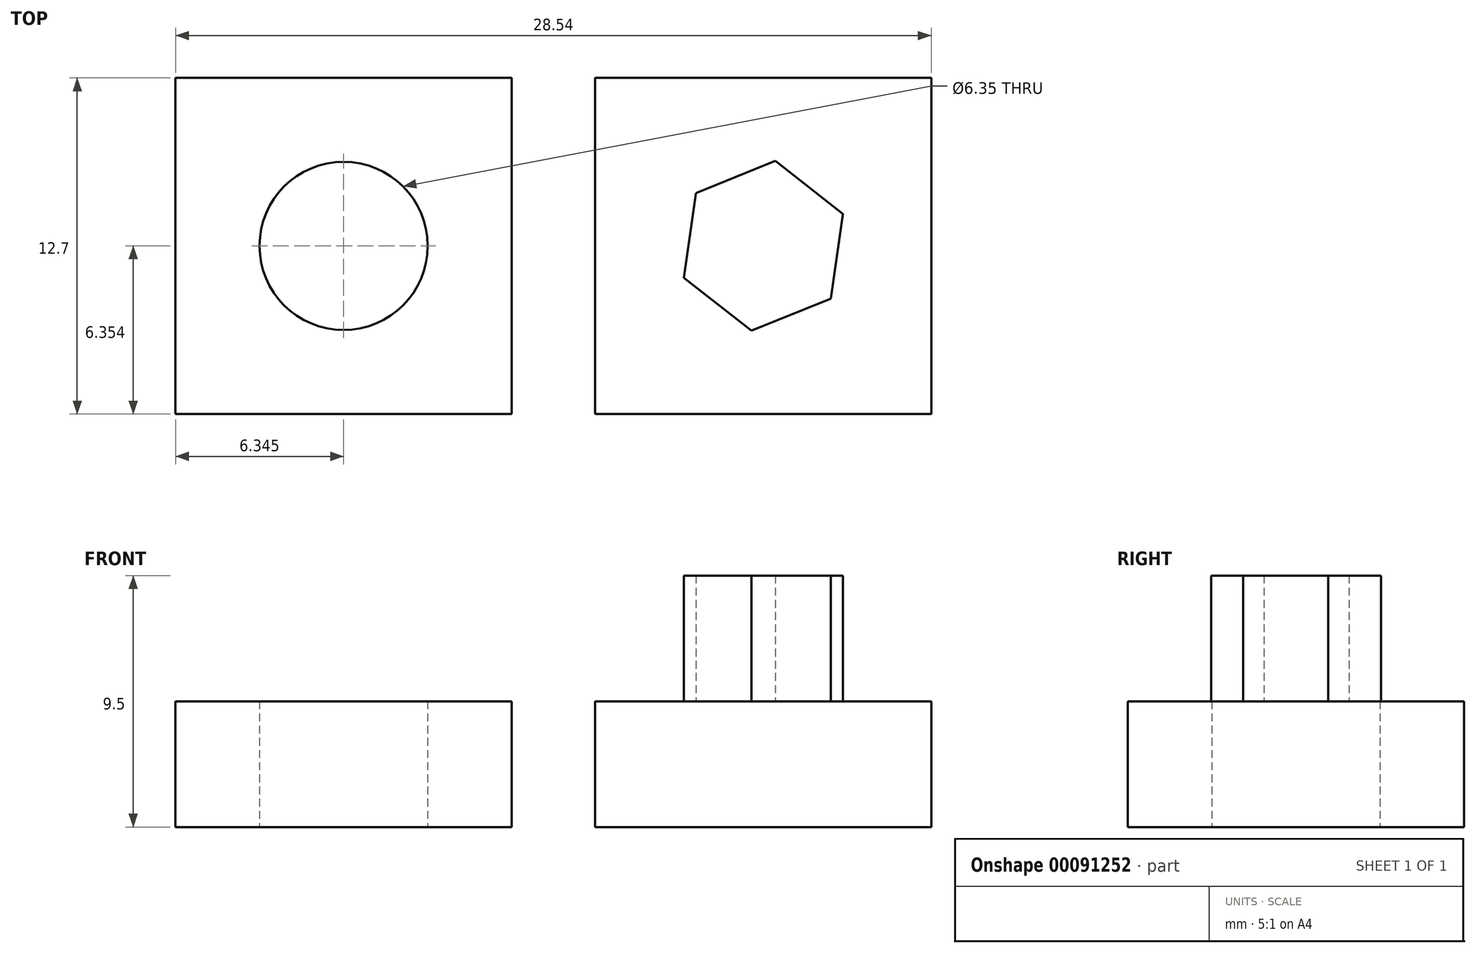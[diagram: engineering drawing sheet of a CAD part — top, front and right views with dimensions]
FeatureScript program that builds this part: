
annotation { "Feature Type Name" : "Feature", "Feature Type Description" : "" }
export const myFeature = defineFeature(function(context is Context, id is Id, definition is map)
    precondition{}
    {
        {
            var Q0;
            Q0=qCreatedBy(makeId("Top.planeOp"),FACE);
            var sketch = newSketch(context, id + "F0", { "sketchPlane" : qUnion([Q0])});
            skLineSegment(sketch, "E0.bottom", {"start": v(-14.27, 2.41) * mm, "end": v(-1.57, 2.41) * mm});
            skLineSegment(sketch, "E0.top", {"start": v(-14.27, -10.29) * mm, "end": v(-1.57, -10.29) * mm});
            skLineSegment(sketch, "E0.left", {"start": v(-14.27, 2.41) * mm, "end": v(-14.27, -10.29) * mm});
            skLineSegment(sketch, "E0.right", {"start": v(-1.57, 2.41) * mm, "end": v(-1.57, -10.29) * mm});
            skLineSegment(sketch, "E1.bottom", {"start": v(1.57, 2.41) * mm, "end": v(14.27, 2.41) * mm});
            skLineSegment(sketch, "E1.top", {"start": v(1.57, -10.29) * mm, "end": v(14.27, -10.29) * mm});
            skLineSegment(sketch, "E1.left", {"start": v(1.57, 2.41) * mm, "end": v(1.57, -10.29) * mm});
            skLineSegment(sketch, "E1.right", {"start": v(14.27, 2.41) * mm, "end": v(14.27, -10.29) * mm});
            skCircle(sketch, "E2", {"center": v(-7.92, -3.94) * mm, "radius": 3.18 * mm});
            skPoint(sketch, "E2.centerSnap0", {"position": v(-7.92, -10.29) * mm});
            skPoint(sketch, "E2.centerSnap1", {"position": v(-14.27, -3.94) * mm});
            skSolve(sketch);
        }
        {
            var Q0;
            Q0 = qSketchRegion(id + "F0", true);
            extrude(context, id + "F1", {"entities" : qUnion([Q0]), "depth" : 4.75 * mm});
        }
        {
            var Q0;
            Q0=makeQuery(id+"F1.opExtrude","CAP_FACE",FACE,{"disambiguationData":[OSD([sQuery(id+"F0.wireOp",EDGE,"E1.bottom"),sQuery(id+"F0.wireOp",EDGE,"E1.top"),sQuery(id+"F0.wireOp",EDGE,"E1.left"),sQuery(id+"F0.wireOp",EDGE,"E1.right")])],"isStart":false});
            var sketch = newSketch(context, id + "F2", { "sketchPlane" : qUnion([Q0])});
            skCircle(sketch, "E3", {"center": v(7.92, -3.94) * mm, "radius": 1.59 * mm, "construction": true});
            skPoint(sketch, "E3.centerSnap0", {"position": v(1.57, -3.94) * mm});
            skPoint(sketch, "E3.centerSnap1", {"position": v(7.92, -10.29) * mm});
            skCircle(sketch, "E4.cCircle", {"center": v(7.92, -3.94) * mm, "radius": 3.24 * mm, "construction": true});
            skLineSegment(sketch, "E4.0", {"start": v(10.93, -2.73) * mm, "end": v(10.47, -5.93) * mm});
            skLineSegment(sketch, "E4.1", {"start": v(10.47, -5.93) * mm, "end": v(7.47, -7.14) * mm});
            skLineSegment(sketch, "E4.2", {"start": v(7.47, -7.14) * mm, "end": v(4.92, -5.15) * mm});
            skLineSegment(sketch, "E4.3", {"start": v(4.92, -5.15) * mm, "end": v(5.38, -1.94) * mm});
            skLineSegment(sketch, "E4.4", {"start": v(5.38, -1.94) * mm, "end": v(8.38, -0.73) * mm});
            skLineSegment(sketch, "E4.5", {"start": v(8.38, -0.73) * mm, "end": v(10.93, -2.73) * mm});
            skSolve(sketch);
        }
        {
            var Q0;
            Q0 = qSketchRegion(id + "F2", true);
            extrude(context, id + "F3", {"entities" : qUnion([Q0]), "operationType" : NewBodyOperationType.ADD, "depth" : 4.75 * mm});
        }
    });
